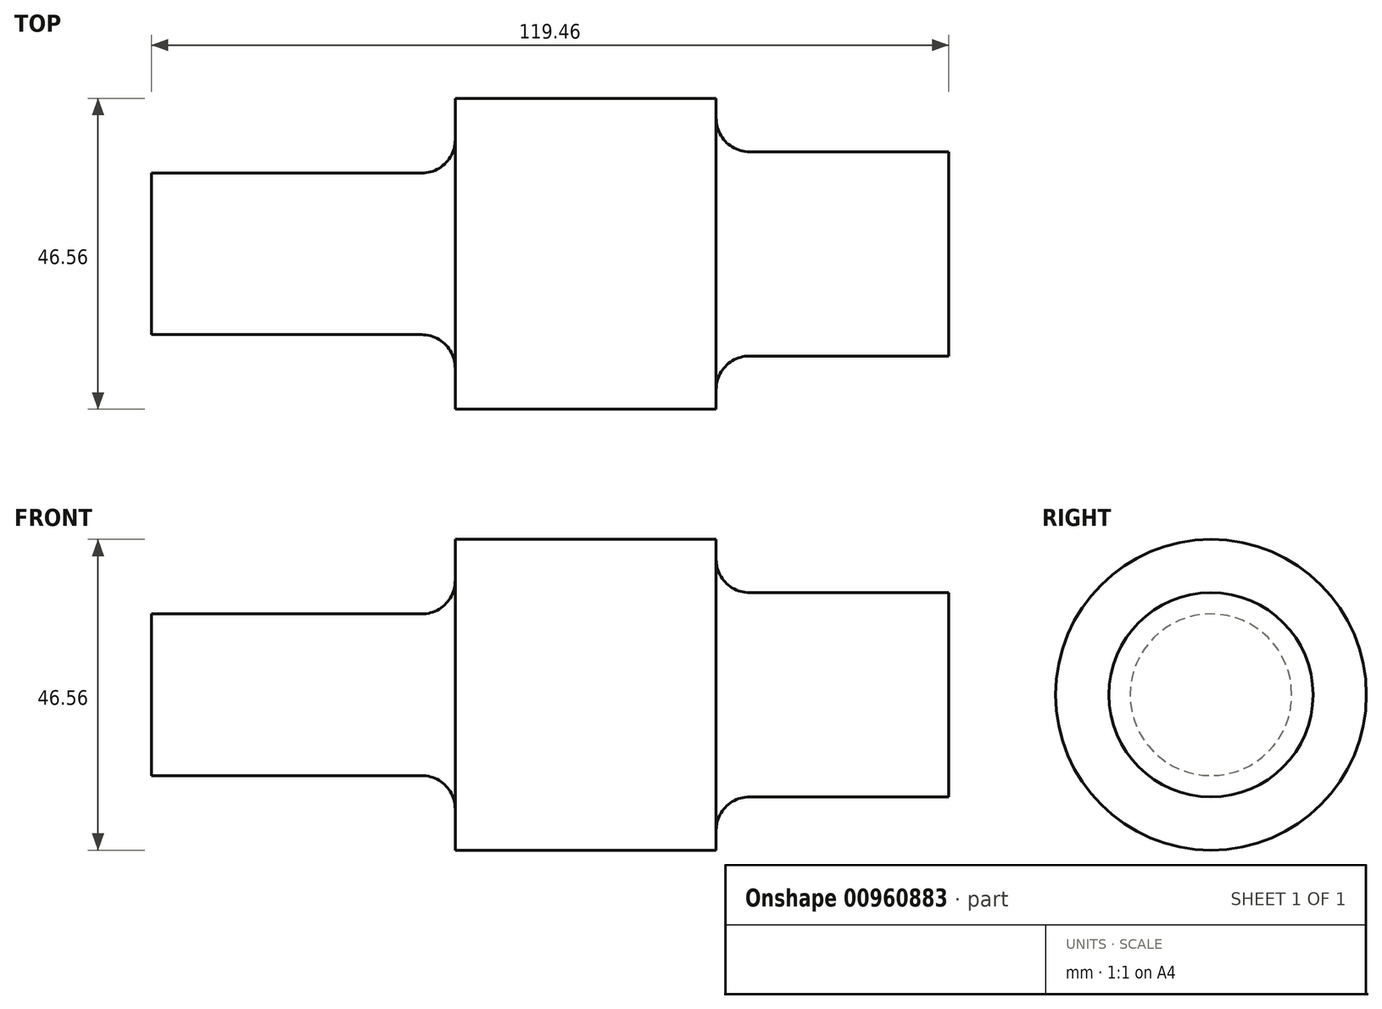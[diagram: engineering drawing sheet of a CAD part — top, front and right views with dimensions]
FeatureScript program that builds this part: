
annotation { "Feature Type Name" : "Feature", "Feature Type Description" : "" }
export const myFeature = defineFeature(function(context is Context, id is Id, definition is map)
    precondition{}
    {
        {
            var Q0;
            Q0=qCreatedBy(makeId("Front.planeOp"),FACE);
            var sketch = newSketch(context, id + "F0", { "sketchPlane" : qUnion([Q0])});
            skLineSegment(sketch, "E0", {"start": v(0, 0) * mm, "end": v(-67.18, 0) * mm});
            skLineSegment(sketch, "E1", {"start": v(-67.18, 0) * mm, "end": v(-67.18, 12.1) * mm});
            skLineSegment(sketch, "E2", {"start": v(-67.18, 12.1) * mm, "end": v(-26.68, 12.1) * mm});
            skLineSegment(sketch, "E3", {"start": v(-21.68, 17.1) * mm, "end": v(-21.68, 23.28) * mm});
            skLineSegment(sketch, "E4", {"start": v(-21.68, 23.28) * mm, "end": v(17.43, 23.28) * mm});
            skLineSegment(sketch, "E5", {"start": v(17.43, 23.28) * mm, "end": v(17.43, 20.3) * mm});
            skLineSegment(sketch, "E6", {"start": v(22.43, 15.3) * mm, "end": v(52.28, 15.3) * mm});
            skLineSegment(sketch, "E7", {"start": v(52.28, 15.3) * mm, "end": v(52.28, 0) * mm});
            skLineSegment(sketch, "E8", {"start": v(52.28, 0) * mm, "end": v(0, 0) * mm});
            skPoint(sketch, "E9.visualSharp", {"position": v(-21.68, 12.1) * mm});
            skArc(sketch, "E9.filletArc", {"start": v(-26.68, 12.1) * mm, "mid": v(-23.15, 13.57) * mm, "end": v(-21.68, 17.1) * mm});
            skPoint(sketch, "E10.visualSharp", {"position": v(17.43, 15.3) * mm});
            skArc(sketch, "E10.filletArc", {"start": v(17.43, 20.3) * mm, "mid": v(18.9, 16.76) * mm, "end": v(22.43, 15.3) * mm});
            skSolve(sketch);
        }
        {
            var Q0;
            Q0=makeQuery(id+"F0.imprint","IMPRINT",FACE,{"disambiguationData":[TD([[makeQuery(id+"F0.imprint","IMPRINT",EDGE,{"derivedFrom":sQuery(id+"F0.wireOp",EDGE,"E0")}),-1.0]])]});
            var Q1;
            Q1=sQuery(id+"F0.wireOp",EDGE,"E0");
            revolve(context, id + "F1", {"surfaceOperationType" : NewSurfaceOperationType.NEW, "entities" : qUnion([Q0]), "axis" : qUnion([Q1]), "revolveType" : RevolveType.FULL});
        }
    });
